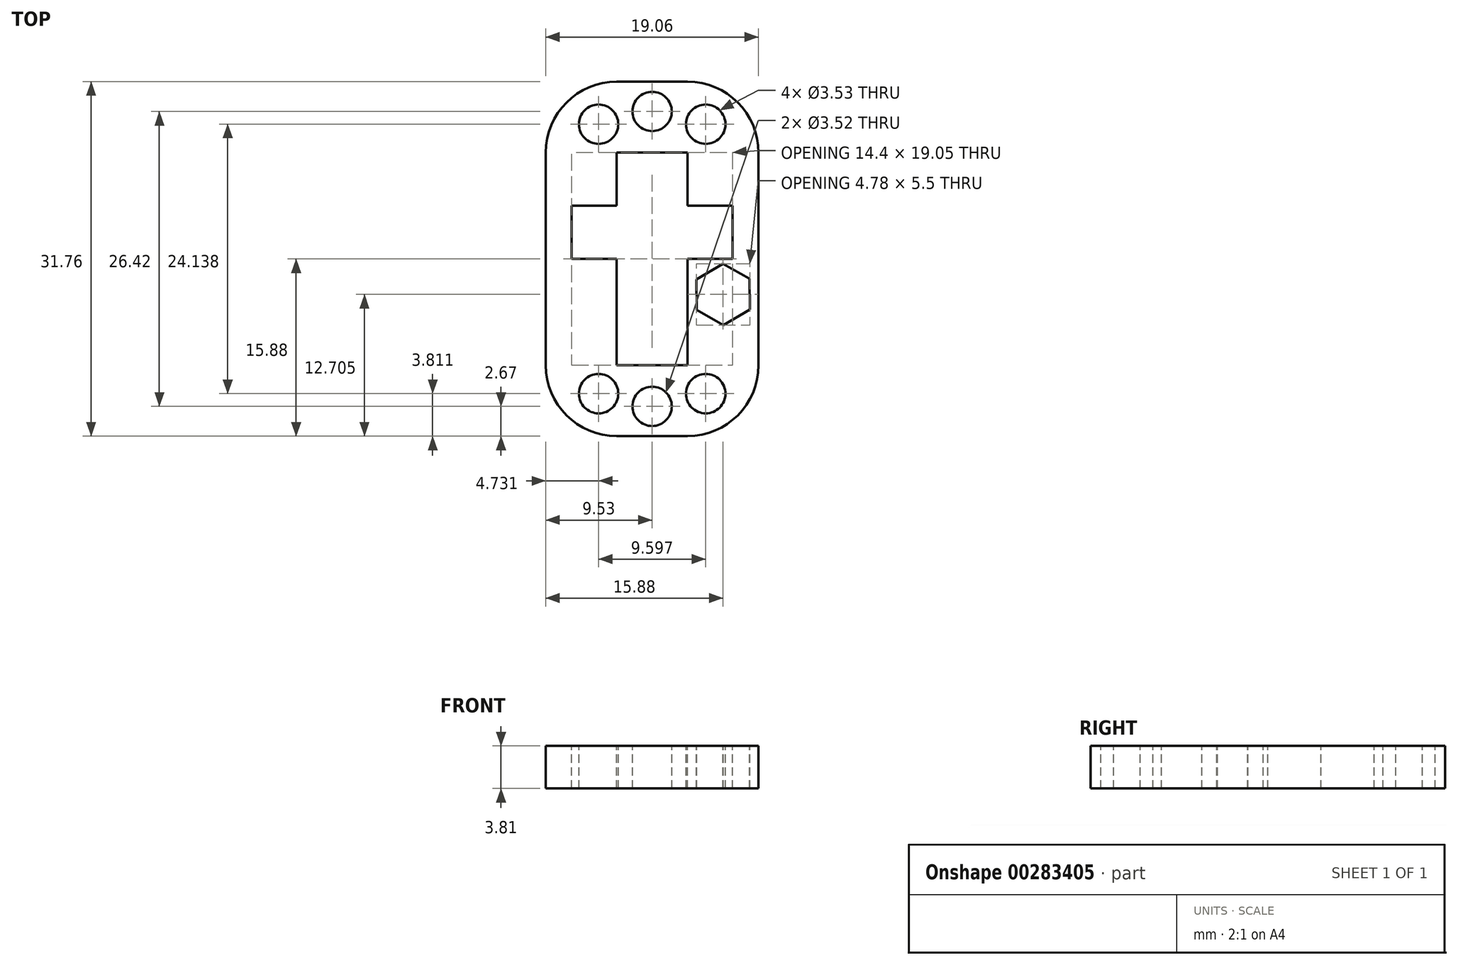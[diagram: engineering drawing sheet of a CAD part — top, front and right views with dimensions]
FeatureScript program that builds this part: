
annotation { "Feature Type Name" : "Feature", "Feature Type Description" : "" }
export const myFeature = defineFeature(function(context is Context, id is Id, definition is map)
    precondition{}
    {
        {
            var Q0;
            Q0=qCreatedBy(makeId("Top.planeOp"),FACE);
            var sketch = newSketch(context, id + "F0", { "sketchPlane" : qUnion([Q0])});
            skLineSegment(sketch, "E0.bottom", {"start": v(3.17, -15.88) * mm, "end": v(-3.18, -15.88) * mm});
            skLineSegment(sketch, "E0.top", {"start": v(3.18, 15.88) * mm, "end": v(-3.17, 15.88) * mm});
            skLineSegment(sketch, "E0.left", {"start": v(9.53, -9.53) * mm, "end": v(9.53, 9.52) * mm});
            skLineSegment(sketch, "E0.right", {"start": v(-9.53, -9.53) * mm, "end": v(-9.53, 9.52) * mm});
            skPoint(sketch, "E0.middle", {"position": v(0, 0) * mm});
            skPoint(sketch, "E1.visualSharp", {"position": v(9.52, -15.88) * mm});
            skArc(sketch, "E1.filletArc", {"start": v(3.18, -15.88) * mm, "mid": v(7.67, -14.02) * mm, "end": v(9.52, -9.53) * mm});
            skPoint(sketch, "E2.visualSharp", {"position": v(-9.53, -15.88) * mm});
            skArc(sketch, "E2.filletArc", {"start": v(-9.53, -9.53) * mm, "mid": v(-7.67, -14.02) * mm, "end": v(-3.18, -15.88) * mm});
            skPoint(sketch, "E3.end.orphan", {"position": v(-6.89, 21.26) * mm});
            skPoint(sketch, "E4.visualSharp", {"position": v(-9.52, 15.88) * mm});
            skArc(sketch, "E4.filletArc", {"start": v(-3.17, 15.87) * mm, "mid": v(-7.67, 14.02) * mm, "end": v(-9.52, 9.52) * mm});
            skPoint(sketch, "E5.visualSharp", {"position": v(9.53, 15.88) * mm});
            skArc(sketch, "E5.filletArc", {"start": v(9.53, 9.52) * mm, "mid": v(7.67, 14.02) * mm, "end": v(3.18, 15.88) * mm});
            skSolve(sketch);
        }
        {
            var Q0;
            Q0=makeQuery(id+"F0.imprint","IMPRINT",FACE,{"disambiguationData":[TD([[makeQuery(id+"F0.imprint","IMPRINT",EDGE,{"derivedFrom":sQuery(id+"F0.wireOp",EDGE,"E0.bottom")}),-1.0]])]});
            var Q1;
            Q1=makeQuery(id+"F0.imprint","IMPRINT",FACE,{"disambiguationData":[TD([[makeQuery(id+"F0.imprint","IMPRINT",EDGE,{"derivedFrom":sQuery(id+"F0.wireOp",EDGE,"E0.top")}),-1.0]])]});
            extrude(context, id + "F1", {"entities" : qUnion([Q0, Q1]), "depth" : 3.8 * mm});
        }
        {
            var Q0;
            Q0=makeQuery(id+"F1.opExtrude","CAP_FACE",FACE,{"disambiguationData":[OSD([sQuery(id+"F0.wireOp",EDGE,"E0.bottom"),sQuery(id+"F0.wireOp",EDGE,"E0.left"),sQuery(id+"F0.wireOp",EDGE,"E0.right"),sQuery(id+"F0.wireOp",EDGE,"E1.filletArc"),sQuery(id+"F0.wireOp",EDGE,"E2.filletArc"),sQuery(id+"F0.wireOp",EDGE,"E3"),sQuery(id+"F0.wireOp",EDGE,"3X1dXW6f-O7UF-HMRr-VSze-Dz3WneAd3JyF"),sQuery(id+"F0.wireOp",EDGE,"bvIZAQ6O-4H2M-6Mhz-PqoI-74Gqt2CO2m6L"),sQuery(id+"F0.wireOp",EDGE,"UphixzXV-ZaX1-nS5S-D3e8-1LdGh0I2YZki")])],"isStart":false});
            var sketch = newSketch(context, id + "F2", { "sketchPlane" : qUnion([Q0])});
            skLineSegment(sketch, "E6.bottom", {"start": v(3.17, -9.53) * mm, "end": v(-3.17, -9.53) * mm});
            skLineSegment(sketch, "E6.top", {"start": v(3.17, 9.53) * mm, "end": v(-3.17, 9.53) * mm});
            skLineSegment(sketch, "E6.left", {"start": v(3.17, -9.53) * mm, "end": v(3.17, 9.53) * mm});
            skLineSegment(sketch, "E6.right", {"start": v(-3.17, -9.53) * mm, "end": v(-3.17, 9.53) * mm});
            skPoint(sketch, "E6.middle", {"position": v(0, 0) * mm});
            skPoint(sketch, "E7.cornerSnap0", {"position": v(9.53, 0) * mm});
            skPoint(sketch, "E7.cornerSnap1", {"position": v(-7.67, -14.02) * mm});
            skLineSegment(sketch, "E8.bottom", {"start": v(7.2, 0) * mm, "end": v(-7.2, 0) * mm});
            skLineSegment(sketch, "E8.top", {"start": v(7.2, 4.76) * mm, "end": v(-7.2, 4.76) * mm});
            skLineSegment(sketch, "E8.left", {"start": v(7.2, 0) * mm, "end": v(7.2, 4.76) * mm});
            skLineSegment(sketch, "E8.right", {"start": v(-7.2, 0) * mm, "end": v(-7.2, 4.76) * mm});
            skPoint(sketch, "E8.middle", {"position": v(0, 2.38) * mm});
            skSolve(sketch);
        }
        {
            var Q0;
            {var subQ0=sQuery(id+"F2.wireOp",EDGE,"E6.top");Q0=makeQuery(id+"F2.imprint","IMPRINT",FACE,{"disambiguationData":[TD([[makeQuery(id+"F2.imprint","IMPRINT",EDGE,{"derivedFrom":subQ0}),1.0]])]});}
            var Q1;
            {var subQ0=sQuery(id+"F2.wireOp",EDGE,"E8.bottom");var subQ1=sQuery(id+"F2.wireOp",EDGE,"E6.left");var subQ2=makeQuery(id+"F2.imprint","INTERSECT",VERTEX,{"derivedFrom":[subQ1,subQ0]});Q1=makeQuery(id+"F2.imprint","IMPRINT",FACE,{"disambiguationData":[TD([[makeQuery(id+"F2.imprint","IMPRINT",EDGE,{"disambiguationData":[TD([[subQ2,-1.0]])],"derivedFrom":subQ1}),1.0]])]});}
            var Q2;
            {var subQ0=sQuery(id+"F2.wireOp",EDGE,"E6.bottom");Q2=makeQuery(id+"F2.imprint","IMPRINT",FACE,{"disambiguationData":[TD([[makeQuery(id+"F2.imprint","IMPRINT",EDGE,{"derivedFrom":subQ0}),-1.0]])]});}
            var Q3;
            {var subQ0=sQuery(id+"F2.wireOp",EDGE,"E6.top");Q3=makeQuery(id+"F2.imprint","IMPRINT",FACE,{"disambiguationData":[TD([[makeQuery(id+"F2.imprint","IMPRINT",EDGE,{"derivedFrom":subQ0}),1.0]])]});}
            var Q4;
            {var subQ5=sQuery(id+"F2.wireOp",EDGE,"E8.right");Q4=makeQuery(id+"F2.imprint","IMPRINT",FACE,{"disambiguationData":[TD([[makeQuery(id+"F2.imprint","IMPRINT",EDGE,{"derivedFrom":subQ5}),-1.0]])]});}
            var Q5;
            {var subQ5=sQuery(id+"F2.wireOp",EDGE,"E8.left");Q5=makeQuery(id+"F2.imprint","IMPRINT",FACE,{"disambiguationData":[TD([[makeQuery(id+"F2.imprint","IMPRINT",EDGE,{"derivedFrom":subQ5}),1.0]])]});}
            extrude(context, id + "F3", {"entities" : qUnion([Q0, Q1, Q2, Q3, Q4, Q5]), "operationType" : NewBodyOperationType.REMOVE, "oppositeDirection" : true, "depth" : 25.4 * mm});
        }
        {
            var Q0;
            {var subQ10=sQuery(id+"F2.wireOp",EDGE,"E6.bottom");Q0=makeQuery(id+"F2.imprint","IMPRINT",FACE,{"disambiguationData":[TD([[makeQuery(id+"F2.imprint","IMPRINT",EDGE,{"derivedFrom":subQ10}),1.0]])]});}
            var sketch = newSketch(context, id + "F4", { "sketchPlane" : qUnion([Q0])});
            skPoint(sketch, "E9", {"position": v(5.45, 12.07) * mm});
            skPoint(sketch, "E10", {"position": v(0, 13.2) * mm});
            skCircle(sketch, "E11", {"center": v(0, 13.2) * mm, "radius": 1.76 * mm});
            skCircle(sketch, "E12.MirrorC", {"center": v(4.8, 12.07) * mm, "radius": 1.77 * mm});
            skPoint(sketch, "E13.orphan", {"position": v(-9.58, 15.93) * mm});
            skPoint(sketch, "E14.end.orphan", {"position": v(9.55, 15.93) * mm});
            skPoint(sketch, "E15.center.orphan", {"position": v(-4.8, 12.07) * mm});
            skCircle(sketch, "E16.MirrorC", {"center": v(-4.8, 12.07) * mm, "radius": 1.77 * mm});
            skCircle(sketch, "E17.MirrorC", {"center": v(-4.8, -12.07) * mm, "radius": 1.77 * mm});
            skCircle(sketch, "E18.MirrorC", {"center": v(0, -13.2) * mm, "radius": 1.76 * mm});
            skCircle(sketch, "E19.MirrorC", {"center": v(4.8, -12.07) * mm, "radius": 1.77 * mm});
            skSolve(sketch);
        }
        {
            var Q0;
            Q0 = qSketchRegion(id + "F4", true);
            extrude(context, id + "F5", {"entities" : qUnion([Q0]), "operationType" : NewBodyOperationType.REMOVE, "oppositeDirection" : true, "depth" : 25.4 * mm});
        }
        {
            var Q0;
            Q0=makeQuery(id+"F1.opExtrude","CAP_FACE",FACE,{"disambiguationData":[OSD([sQuery(id+"F0.wireOp",EDGE,"E0.bottom"),sQuery(id+"F0.wireOp",EDGE,"E0.top"),sQuery(id+"F0.wireOp",EDGE,"E0.left"),sQuery(id+"F0.wireOp",EDGE,"E0.right"),sQuery(id+"F0.wireOp",EDGE,"E1.filletArc"),sQuery(id+"F0.wireOp",EDGE,"E2.filletArc"),sQuery(id+"F0.wireOp",EDGE,"E4.filletArc"),sQuery(id+"F0.wireOp",EDGE,"E5.filletArc")])],"isStart":false});
            var sketch = newSketch(context, id + "F6", { "sketchPlane" : qUnion([Q0])});
            skCircle(sketch, "E20.cCircle", {"center": v(6.35, -3.18) * mm, "radius": 2.75 * mm, "construction": true});
            skLineSegment(sketch, "E20.0", {"start": v(8.74, -4.53) * mm, "end": v(6.37, -5.92) * mm});
            skLineSegment(sketch, "E20.1", {"start": v(6.37, -5.92) * mm, "end": v(3.98, -4.57) * mm});
            skLineSegment(sketch, "E20.2", {"start": v(3.98, -4.57) * mm, "end": v(3.96, -1.82) * mm});
            skLineSegment(sketch, "E20.3", {"start": v(3.96, -1.82) * mm, "end": v(6.33, -0.43) * mm});
            skLineSegment(sketch, "E20.4", {"start": v(6.33, -0.43) * mm, "end": v(8.72, -1.78) * mm});
            skLineSegment(sketch, "E20.5", {"start": v(8.72, -1.78) * mm, "end": v(8.74, -4.53) * mm});
            skLineSegment(sketch, "E21", {"start": v(3.17, -3.18) * mm, "end": v(9.53, -3.18) * mm, "construction": true});
            skSolve(sketch);
        }
        {
            var Q0;
            Q0=makeQuery(id+"F6.imprint","IMPRINT",FACE,{"disambiguationData":[TD([[makeQuery(id+"F6.imprint","IMPRINT",EDGE,{"derivedFrom":sQuery(id+"F6.wireOp",EDGE,"E20.0")}),-1.0]])]});
            extrude(context, id + "F7", {"entities" : qUnion([Q0]), "operationType" : NewBodyOperationType.REMOVE, "oppositeDirection" : true, "depth" : 25.4 * mm});
        }
    });
